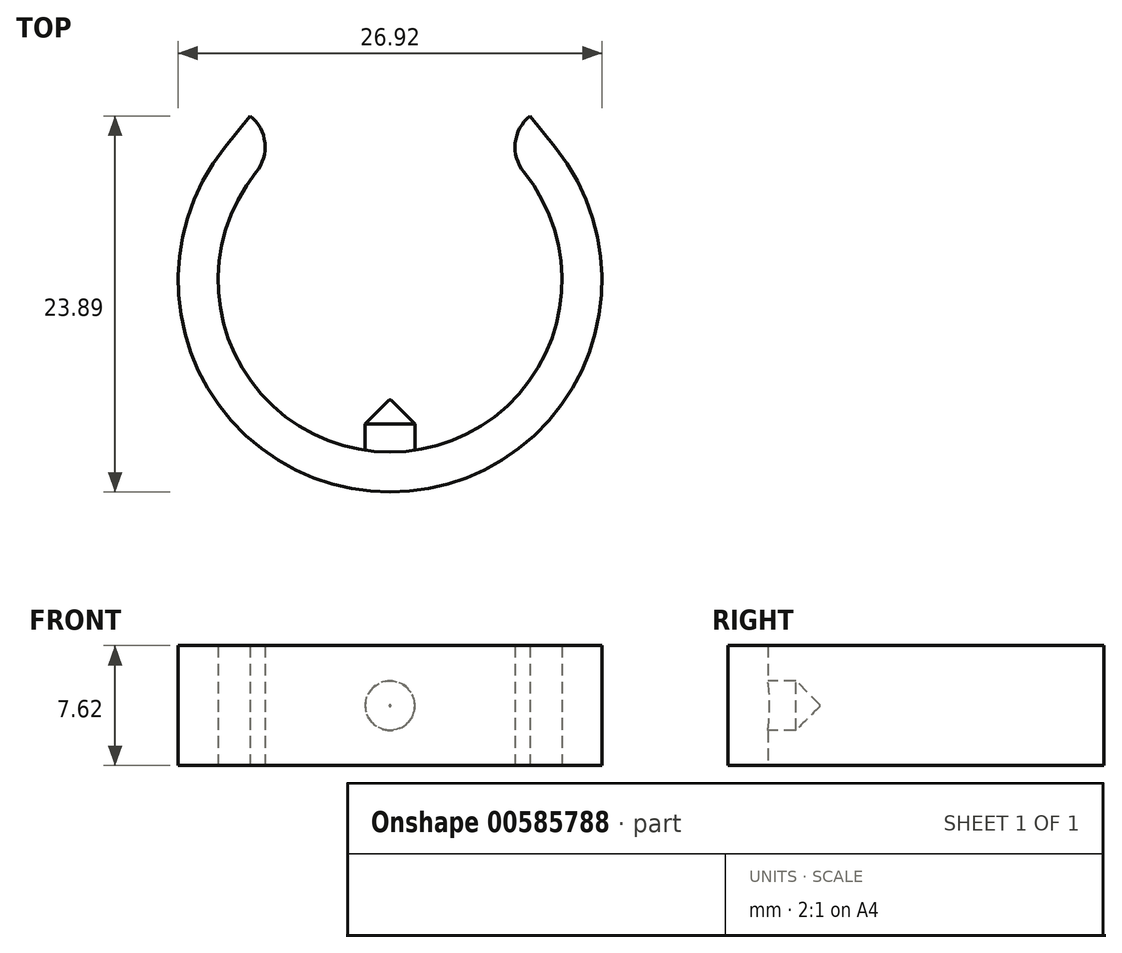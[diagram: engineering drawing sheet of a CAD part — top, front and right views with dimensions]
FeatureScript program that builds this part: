
annotation { "Feature Type Name" : "Feature", "Feature Type Description" : "" }
export const myFeature = defineFeature(function(context is Context, id is Id, definition is map)
    precondition{}
    {
        {
            var Q0;
            Q0=qCreatedBy(makeId("Top.planeOp"),FACE);
            var sketch = newSketch(context, id + "F0", { "sketchPlane" : qUnion([Q0])});
            skArc(sketch, "E0", {"start": v(-8.5, 6.86) * mm, "mid": v(0, -10.92) * mm, "end": v(8.5, 6.86) * mm});
            skArc(sketch, "E1", {"start": v(10.48, 8.45) * mm, "mid": v(0, -13.46) * mm, "end": v(-10.48, 8.45) * mm});
            skArc(sketch, "E2", {"start": v(-8.5, 6.86) * mm, "mid": v(-7.95, 8.72) * mm, "end": v(-8.88, 10.43) * mm});
            skArc(sketch, "E3", {"start": v(8.5, 6.86) * mm, "mid": v(7.95, 8.72) * mm, "end": v(8.88, 10.43) * mm});
            skLineSegment(sketch, "E4", {"start": v(-10.48, 8.45) * mm, "end": v(-8.88, 10.43) * mm});
            skLineSegment(sketch, "E5", {"start": v(10.48, 8.45) * mm, "end": v(8.88, 10.43) * mm});
            skSolve(sketch);
        }
        {
            var Q0;
            Q0 = qSketchRegion(id + "F0", true);
            extrude(context, id + "F1", {"entities" : qUnion([Q0]), "depth" : 7.62 * mm, "offsetDistance" : 25.4 * mm});
        }
        {
            var Q0;
            Q0=qCreatedBy(makeId("Front.planeOp"),FACE);
            cPlane(context, id + "F2", {"entities" : qUnion([Q0]), "cplaneType" : CPlaneType.OFFSET, "offset" : 11.43 * mm, "width" : 152.4 * mm, "height" : 152.4 * mm});
        }
        {
            var Q0;
            Q0=qCreatedBy(id+"F2.planeOp",FACE);
            var sketch = newSketch(context, id + "F3", { "sketchPlane" : qUnion([Q0])});
            skCircle(sketch, "E6", {"center": v(0, 3.81) * mm, "radius": 1.57 * mm});
            skSolve(sketch);
        }
        {
            var Q0;
            Q0 = qSketchRegion(id + "F3", true);
            extrude(context, id + "F4", {"entities" : qUnion([Q0]), "operationType" : NewBodyOperationType.ADD, "oppositeDirection" : true, "depth" : 3.8 * mm, "offsetDistance" : 25.4 * mm});
        }
        {
            var Q0;
            Q0=makeQuery(id+"F4.opExtrude","CAP_EDGE",EDGE,{"disambiguationData":[OSD([sQuery(id+"F3.wireOp",EDGE,"E6")])],"isStart":false});
            chamfer(context, id + "F5", {"entities" : qUnion([Q0]), "width" : 1.52 * mm, "tangentPropagation" : true});
        }
    });
